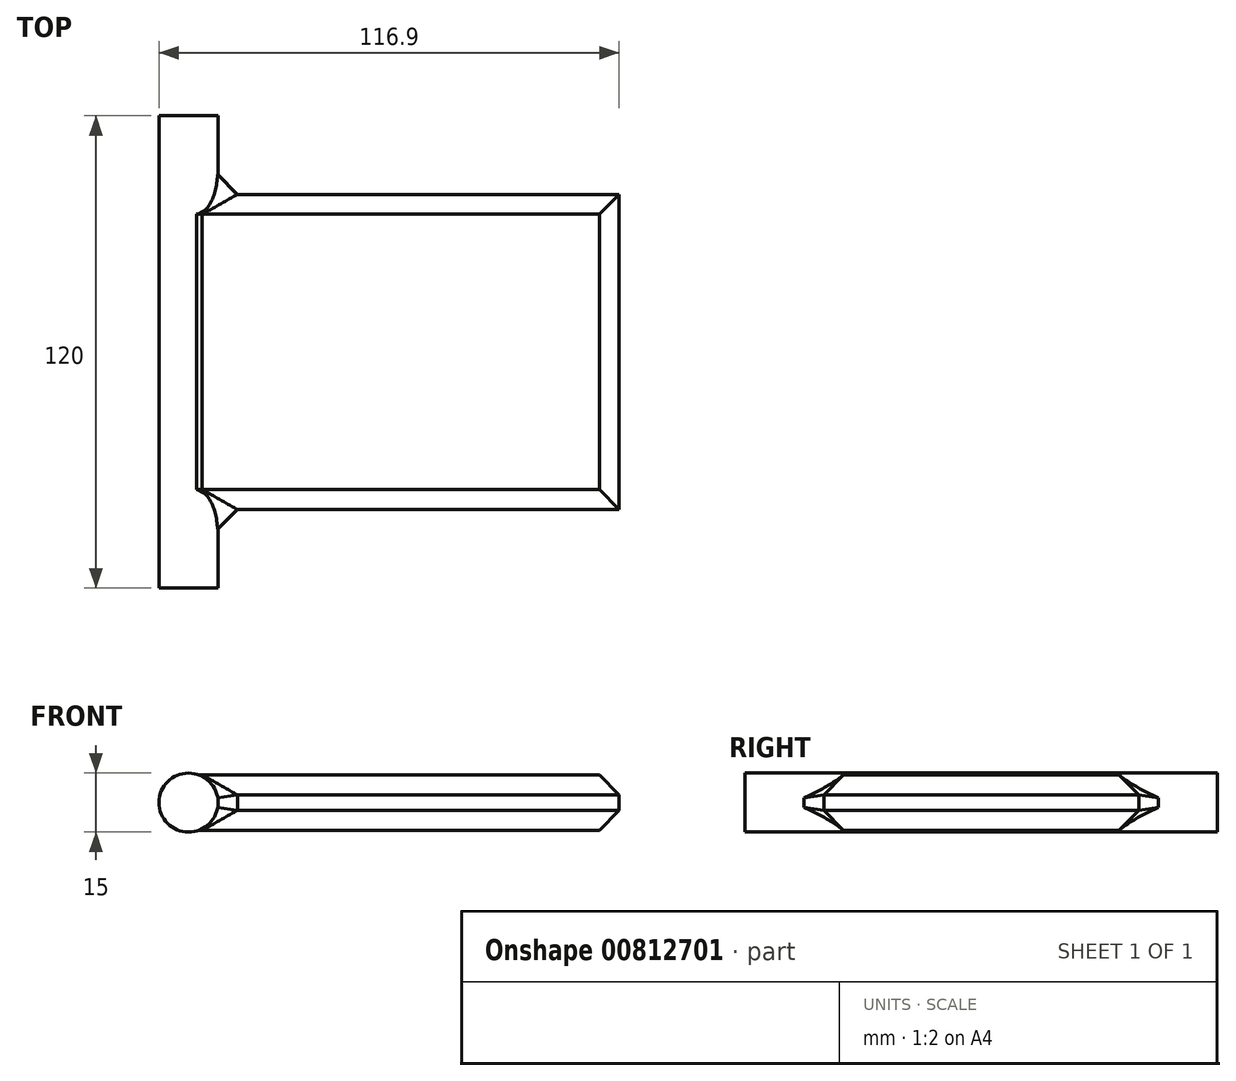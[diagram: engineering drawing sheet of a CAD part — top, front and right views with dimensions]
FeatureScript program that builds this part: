
annotation { "Feature Type Name" : "Feature", "Feature Type Description" : "" }
export const myFeature = defineFeature(function(context is Context, id is Id, definition is map)
    precondition{}
    {
        {
            var Q0;
            Q0=qCreatedBy(makeId("Front.planeOp"),FACE);
            var sketch = newSketch(context, id + "F0", { "sketchPlane" : qUnion([Q0])});
            skCircle(sketch, "E0", {"center": v(-59.4, 0) * mm, "radius": 7.5 * mm});
            skSolve(sketch);
        }
        {
            var Q0;
            Q0 = qSketchRegion(id + "F0", true);
            var Q1;
            Q1 = qSketchRegion(id + "F3", true);
            extrude(context, id + "F1", {"entities" : qUnion([Q0, Q1]), "depth" : 60 * mm, "offsetDistance" : 25 * mm, "hasSecondDirection" : true, "secondDirectionOppositeDirection" : true, "secondDirectionDepth" : 60 * mm});
        }
        {
            var Q0;
            Q0=qCreatedBy(makeId("Right.planeOp"),FACE);
            cPlane(context, id + "F2", {"entities" : qUnion([Q0]), "cplaneType" : CPlaneType.OFFSET, "offset" : 50 * mm, "width" : 150 * mm, "height" : 150 * mm});
        }
        {
            var Q0;
            Q0=qCreatedBy(id+"F2.planeOp",FACE);
            var sketch = newSketch(context, id + "F3", { "sketchPlane" : qUnion([Q0])});
            skLineSegment(sketch, "E1.bottom", {"start": v(-40, 7) * mm, "end": v(40, 7) * mm});
            skLineSegment(sketch, "E1.top", {"start": v(-40, -7) * mm, "end": v(40, -7) * mm});
            skLineSegment(sketch, "E1.left", {"start": v(-40, 7) * mm, "end": v(-40, -7) * mm});
            skLineSegment(sketch, "E1.right", {"start": v(40, 7) * mm, "end": v(40, -7) * mm});
            skSolve(sketch);
        }
        {
            var Q0;
            Q0 = qSketchRegion(id + "F3", true);
            extrude(context, id + "F4", {"entities" : qUnion([Q0]), "operationType" : NewBodyOperationType.ADD, "endBound" : BoundingType.UP_TO_NEXT, "oppositeDirection" : true, "depth" : 25 * mm, "offsetDistance" : 25 * mm});
        }
        {
            var Q0;
            Q0=makeQuery(id+"F4.opExtrude","SWEPT_FACE",FACE,{"disambiguationData":[OSD([sQuery(id+"F3.wireOp",EDGE,"E1.bottom")])]});
            var Q1;
            Q1=makeQuery(id+"F4.opExtrude","SWEPT_FACE",FACE,{"disambiguationData":[OSD([sQuery(id+"F3.wireOp",EDGE,"E1.top")])]});
            chamfer(context, id + "F5", {"entities" : qUnion([Q0, Q1]), "width" : 5 * mm, "tangentPropagation" : true});
        }
    });
